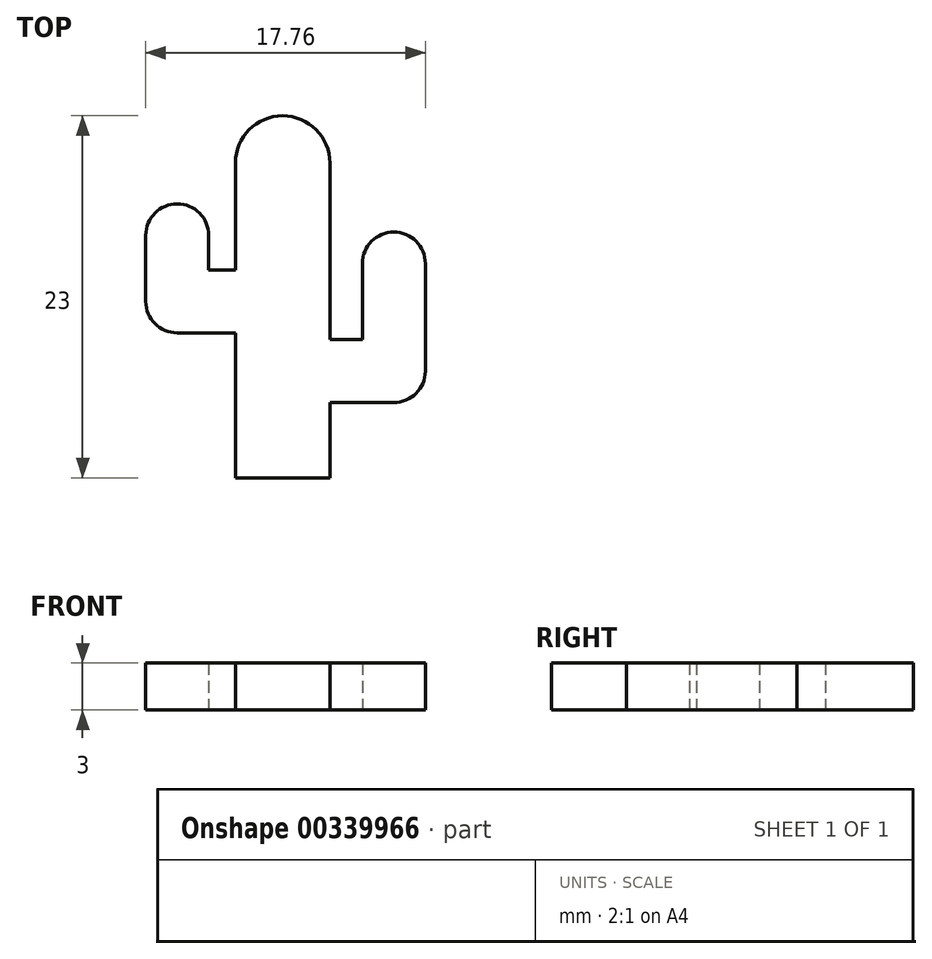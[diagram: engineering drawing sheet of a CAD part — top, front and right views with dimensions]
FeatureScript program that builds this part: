
annotation { "Feature Type Name" : "Feature", "Feature Type Description" : "" }
export const myFeature = defineFeature(function(context is Context, id is Id, definition is map)
    precondition{}
    {
        {
            var Q0;
            Q0=qCreatedBy(makeId("Top.planeOp"),FACE);
            var sketch = newSketch(context, id + "F0", { "sketchPlane" : qUnion([Q0])});
            skCircle(sketch, "E0", {"center": v(0, 0) * mm, "radius": 3 * mm});
            skLineSegment(sketch, "E1.bottom", {"start": v(-3, 0) * mm, "end": v(3, 0) * mm});
            skLineSegment(sketch, "E1.top", {"start": v(-3, -20) * mm, "end": v(3, -20) * mm});
            skLineSegment(sketch, "E1.left", {"start": v(-3, 0) * mm, "end": v(-3, -20) * mm});
            skLineSegment(sketch, "E1.right", {"start": v(3, 0) * mm, "end": v(3, -20) * mm});
            skLineSegment(sketch, "E2.bottom", {"start": v(3, -11.21) * mm, "end": v(5.06, -11.21) * mm});
            skLineSegment(sketch, "E2.top", {"start": v(3, -15.21) * mm, "end": v(5.06, -15.21) * mm});
            skLineSegment(sketch, "E2.left", {"start": v(3, -11.21) * mm, "end": v(3, -15.21) * mm});
            skLineSegment(sketch, "E2.right", {"start": v(5.06, -11.21) * mm, "end": v(5.06, -15.21) * mm});
            skLineSegment(sketch, "E3.bottom", {"start": v(5.06, -15.21) * mm, "end": v(9.06, -15.21) * mm});
            skLineSegment(sketch, "E3.top", {"start": v(5.06, -6.39) * mm, "end": v(9.06, -6.39) * mm});
            skLineSegment(sketch, "E3.left", {"start": v(5.06, -15.21) * mm, "end": v(5.06, -6.39) * mm});
            skLineSegment(sketch, "E3.right", {"start": v(9.06, -15.21) * mm, "end": v(9.06, -6.39) * mm});
            skCircle(sketch, "E4", {"center": v(7.06, -6.39) * mm, "radius": 2 * mm});
            skLineSegment(sketch, "E5.bottom", {"start": v(-3, -10.8) * mm, "end": v(-4.7, -10.8) * mm});
            skLineSegment(sketch, "E5.top", {"start": v(-3, -6.8) * mm, "end": v(-4.7, -6.8) * mm});
            skLineSegment(sketch, "E5.left", {"start": v(-3, -10.8) * mm, "end": v(-3, -6.8) * mm});
            skLineSegment(sketch, "E5.right", {"start": v(-4.7, -10.8) * mm, "end": v(-4.7, -6.8) * mm});
            skLineSegment(sketch, "E6.bottom", {"start": v(-4.7, -10.8) * mm, "end": v(-8.7, -10.8) * mm});
            skLineSegment(sketch, "E6.top", {"start": v(-4.7, -4.6) * mm, "end": v(-8.7, -4.6) * mm});
            skLineSegment(sketch, "E6.left", {"start": v(-4.7, -10.8) * mm, "end": v(-4.7, -4.6) * mm});
            skLineSegment(sketch, "E6.right", {"start": v(-8.7, -10.8) * mm, "end": v(-8.7, -4.6) * mm});
            skCircle(sketch, "E7", {"center": v(-6.7, -4.6) * mm, "radius": 2 * mm});
            skSolve(sketch);
        }
        {
            var Q0;
            Q0 = qSketchRegion(id + "F0", true);
            extrude(context, id + "F1", {"entities" : qUnion([Q0]), "depth" : 3 * mm, "offsetDistance" : 25 * mm});
        }
        {
            var Q0;
            Q0=makeQuery(id+"F1.opExtrude","SWEPT_EDGE",EDGE,{"disambiguationData":[OSD([sQuery(id+"F0.wireOp",EDGE,"E6.bottom"),sQuery(id+"F0.wireOp",EDGE,"E6.right")])]});
            var Q1;
            Q1=makeQuery(id+"F1.opExtrude","SWEPT_EDGE",EDGE,{"disambiguationData":[OSD([sQuery(id+"F0.wireOp",EDGE,"E3.bottom"),sQuery(id+"F0.wireOp",EDGE,"E3.right")])]});
            fillet(context, id + "F2", {"entities" : qUnion([Q0, Q1]), "radius" : 2 * mm, "tangentPropagation" : true, "allowEdgeOverflow" : false});
        }
    });
